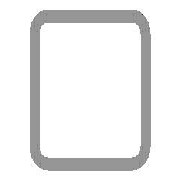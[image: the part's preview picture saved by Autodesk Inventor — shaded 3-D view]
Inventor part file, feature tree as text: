
AUTODESK INVENTOR PART (.ipt)
format: ipt  version: 2025.1 (Build 291241020, 241B)  size: 142,848 bytes
history: native  units: mm (DEFAULTED — no unit token found)
features: other x4, sketch x1, plane x1
ambient origin geometry x8: Origin, YZ Plane, XZ Plane, XY Plane, X Axis, Y Axis, Z Axis, Center Point
bodies: Solid1 (feature_tree), Body (feature_tree)
feature tree (6):
  parser-record x1  (decoder bookkeeping rows leaked as tree rows — omitted from the tree; the rows remain in map.json)
  other  "Driven Length"
  other  "Start plane"
  other  "End plane"
  sketch  "Sketch3"  dims[d3=2750.0mm d4=0.0mm d7=6.0mm d9=100.0mm d11=100.0mm d12=3.0mm d13=-0.0mm d14=2750.0mm d15=50.0mm d16=50.0mm d17=90.0deg d18=2750.0mm]
  plane  "Work Plane3"
